# Revit family: BNB4
name_source: partatom
category: Lighting Fixtures
revit_build: Autodesk Revit 2013 (Build: 20130531_2115(x64)
units: mm (PartAtom-declared; Revit-internal decimal feet)

## types (1)
- BNB4
    Apparent Load = 0 VA
    Assembly Code = D5020200
    Body Material = Metal-Kim Lighting-Aluminum Alloy
    Color Filter = 16777215
    Description = Low Level Luminaire
    Dimming Lamp Color Temperature Shift = <None>
    Emit Shape Visible in Rendering = No
    Emit from Circle Diameter = 6"
    Finish = All colors shall be a Super TGIC thermoset polyester powder coat paint
    Full Load Current = 0 A
    Glass Material = Glass-Kim Lighting-Clear
    Housing Material = Metal-Kim Lighting-Aluminum Alloy
    Initial Lumens = 0 lm
    Lamp = LED
    Lighting Source Height = 38"
    Load Classification = Lighting
    Manufacturer = Kim Lighting
    Manufacturer Fax = 626-369-2695
    MasterFormat Title = Landscape Lighting, Site Lighting, Walkway Lighting
    Model = Bounce Bollard
    Note Text = LF
    Note Visible = Yes
    Number of Poles = 1
    Photometric Notes = More IES files download on Photometric Web Link
    Photometric Web File = bnb-18l3k.ies
    Photometric Web Link = http://www.kimlighting.com
    Power Factor = 1
    Product Documentation Link = http://www.kimlighting.com
    Product Page URL = http://www.kimlighting.com
    Revision Date = 10/17/2017
    Series = Bounce Bollard Luminaire
    Tilt Angle = 90.00°
    Type Comments = Lighting Fixture
    URL = http://www.kimlighting.com
    Voltage = 208 V
    Wattage Comments = 21,31 & 41 Watts

## geometry (parser evidence)
native form markers: Blend x12, Sweep x3
no freeform markers — native parametric forms only
